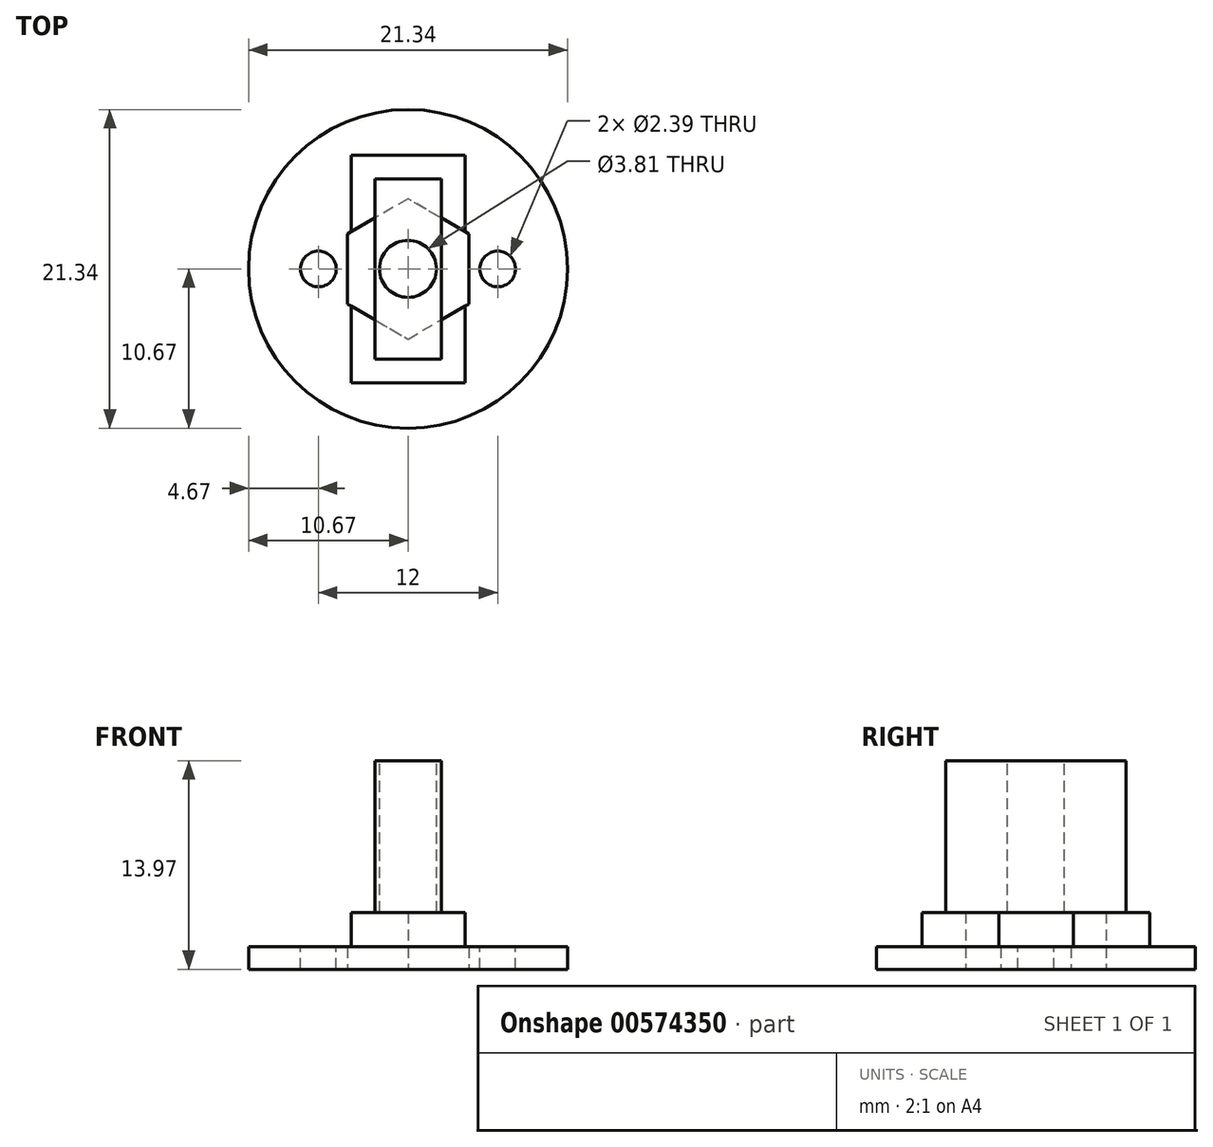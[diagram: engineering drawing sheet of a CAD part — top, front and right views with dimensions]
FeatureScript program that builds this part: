
annotation { "Feature Type Name" : "Feature", "Feature Type Description" : "" }
export const myFeature = defineFeature(function(context is Context, id is Id, definition is map)
    precondition{}
    {
        {
            var Q0;
            Q0=qCreatedBy(makeId("Top.planeOp"),FACE);
            var sketch = newSketch(context, id + "F0", { "sketchPlane" : qUnion([Q0])});
            skCircle(sketch, "E0", {"center": v(0, 0) * mm, "radius": 10.67 * mm});
            skSolve(sketch);
        }
        {
            var Q0;
            Q0 = qSketchRegion(id + "F0", true);
            extrude(context, id + "F1", {"entities" : qUnion([Q0]), "depth" : 1.5 * mm, "offsetDistance" : 25.4 * mm});
        }
        {
            var Q0;
            Q0=makeQuery(id+"F1.opExtrude","CAP_FACE",FACE,{"disambiguationData":[OSD([sQuery(id+"F0.wireOp",EDGE,"E0")])],"isStart":false});
            var sketch = newSketch(context, id + "F2", { "sketchPlane" : qUnion([Q0])});
            skLineSegment(sketch, "E1.bottom", {"start": v(-3.81, 7.62) * mm, "end": v(3.8, 7.62) * mm});
            skLineSegment(sketch, "E1.top", {"start": v(-3.81, -7.62) * mm, "end": v(3.81, -7.62) * mm});
            skLineSegment(sketch, "E1.left", {"start": v(-3.8, 7.62) * mm, "end": v(-3.81, -7.62) * mm});
            skLineSegment(sketch, "E1.right", {"start": v(3.81, 7.62) * mm, "end": v(3.8, -7.62) * mm});
            skLineSegment(sketch, "E2", {"start": v(0, 7.62) * mm, "end": v(0, -7.62) * mm, "construction": true});
            skLineSegment(sketch, "E3", {"start": v(-3.8, 0) * mm, "end": v(3.81, 0) * mm, "construction": true});
            skSolve(sketch);
        }
        {
            var Q0;
            Q0=makeQuery(id+"F2.imprint","IMPRINT",FACE,{"disambiguationData":[TD([[makeQuery(id+"F2.imprint","IMPRINT",EDGE,{"derivedFrom":sQuery(id+"F2.wireOp",EDGE,"E1.bottom")}),-1.0]])]});
            extrude(context, id + "F3", {"entities" : qUnion([Q0]), "operationType" : NewBodyOperationType.ADD, "depth" : 3.8 * mm - 1.5 * mm, "offsetDistance" : 25.4 * mm});
        }
        {
            var Q0;
            Q0=makeQuery(id+"F3.opExtrude","CAP_FACE",FACE,{"disambiguationData":[OSD([sQuery(id+"F2.wireOp",EDGE,"E1.bottom"),sQuery(id+"F2.wireOp",EDGE,"E1.top"),sQuery(id+"F2.wireOp",EDGE,"E1.left"),sQuery(id+"F2.wireOp",EDGE,"E1.right")])],"isStart":false});
            var sketch = newSketch(context, id + "F4", { "sketchPlane" : qUnion([Q0])});
            skLineSegment(sketch, "E4.bottom", {"start": v(-2.22, 6.03) * mm, "end": v(2.22, 6.03) * mm});
            skLineSegment(sketch, "E4.top", {"start": v(-2.22, -6.03) * mm, "end": v(2.22, -6.03) * mm});
            skLineSegment(sketch, "E4.left", {"start": v(-2.22, 6.03) * mm, "end": v(-2.22, -6.03) * mm});
            skLineSegment(sketch, "E4.right", {"start": v(2.22, 6.03) * mm, "end": v(2.22, -6.03) * mm});
            skLineSegment(sketch, "E5", {"start": v(0, 6.03) * mm, "end": v(0, 0) * mm, "construction": true});
            skLineSegment(sketch, "E6", {"start": v(0, 0) * mm, "end": v(-2.22, 0) * mm, "construction": true});
            skSolve(sketch);
        }
        {
            var Q0;
            Q0 = qSketchRegion(id + "F4", true);
            extrude(context, id + "F5", {"entities" : qUnion([Q0]), "operationType" : NewBodyOperationType.ADD, "depth" : 10.16 * mm, "offsetDistance" : 25.4 * mm});
        }
        {
            var Q0;
            Q0=makeQuery(id+"F5.opExtrude","CAP_FACE",FACE,{"disambiguationData":[OSD([sQuery(id+"F4.wireOp",EDGE,"E4.bottom"),sQuery(id+"F4.wireOp",EDGE,"E4.top"),sQuery(id+"F4.wireOp",EDGE,"E4.left"),sQuery(id+"F4.wireOp",EDGE,"E4.right")])],"isStart":false});
            var sketch = newSketch(context, id + "F6", { "sketchPlane" : qUnion([Q0])});
            skCircle(sketch, "E7", {"center": v(0, 0) * mm, "radius": 1.9 * mm});
            skSolve(sketch);
        }
        {
            var Q0;
            Q0 = qSketchRegion(id + "F6", true);
            extrude(context, id + "F7", {"entities" : qUnion([Q0]), "operationType" : NewBodyOperationType.REMOVE, "endBound" : BoundingType.THROUGH_ALL, "oppositeDirection" : true, "depth" : 25.4 * mm, "offsetDistance" : 25.4 * mm});
        }
        {
            var Q0;
            Q0=makeQuery(id+"F1.opExtrude","CAP_FACE",FACE,{"disambiguationData":[OSD([sQuery(id+"F0.wireOp",EDGE,"E0")])],"isStart":true});
            var sketch = newSketch(context, id + "F8", { "sketchPlane" : qUnion([Q0])});
            skCircle(sketch, "E8.cCircle", {"center": v(0, 0) * mm, "radius": 4.06 * mm, "construction": true});
            skLineSegment(sketch, "E8.0", {"start": v(0, 4.7) * mm, "end": v(4.06, 2.35) * mm});
            skLineSegment(sketch, "E8.1", {"start": v(4.06, 2.35) * mm, "end": v(4.06, -2.35) * mm});
            skLineSegment(sketch, "E8.2", {"start": v(4.06, -2.35) * mm, "end": v(0, -4.7) * mm});
            skLineSegment(sketch, "E8.3", {"start": v(0, -4.7) * mm, "end": v(-4.06, -2.35) * mm});
            skLineSegment(sketch, "E8.4", {"start": v(-4.06, -2.35) * mm, "end": v(-4.06, 2.35) * mm});
            skLineSegment(sketch, "E8.5", {"start": v(-4.06, 2.35) * mm, "end": v(0, 4.7) * mm});
            skPoint(sketch, "E8.0.midPoint", {"position": v(2.03, 3.52) * mm});
            skSolve(sketch);
        }
        {
            var Q0;
            Q0=makeQuery(id+"F8.imprint","IMPRINT",FACE,{"disambiguationData":[TD([[makeQuery(id+"F8.imprint","IMPRINT",EDGE,{"derivedFrom":makeQuery(id+"F7.boolean.opBoolean","INTERSECT",EDGE,{"derivedFrom":[makeQuery(id+"F1.opExtrude","CAP_FACE",FACE,{"disambiguationData":[OSD([sQuery(id+"F0.wireOp",EDGE,"E0")])],"isStart":true}),makeQuery(id+"F7.opExtrude","SWEPT_FACE",FACE,{"disambiguationData":[OSD([sQuery(id+"F6.wireOp",EDGE,"E7")])]})]})}),-1.0]])]});
            var Q1;
            Q1=makeQuery(id+"F8.imprint","IMPRINT",FACE,{"disambiguationData":[TD([[makeQuery(id+"F8.imprint","IMPRINT",EDGE,{"derivedFrom":sQuery(id+"F8.wireOp",EDGE,"E8.0")}),-1.0]])]});
            extrude(context, id + "F9", {"entities" : qUnion([Q0, Q1]), "operationType" : NewBodyOperationType.REMOVE, "oppositeDirection" : true, "depth" : 3.8 * mm, "offsetDistance" : 25.4 * mm});
        }
        {
            var Q0;
            Q0=makeQuery(id+"F1.opExtrude","CAP_FACE",FACE,{"disambiguationData":[OSD([sQuery(id+"F0.wireOp",EDGE,"E0")])],"isStart":false});
            var sketch = newSketch(context, id + "F10", { "sketchPlane" : qUnion([Q0])});
            skCircle(sketch, "E9", {"center": v(-6, 0) * mm, "radius": 1.2 * mm});
            skCircle(sketch, "E10", {"center": v(6, 0) * mm, "radius": 1.2 * mm});
            skSolve(sketch);
        }
        {
            var Q0;
            Q0 = qSketchRegion(id + "F10", true);
            extrude(context, id + "F11", {"entities" : qUnion([Q0]), "operationType" : NewBodyOperationType.REMOVE, "endBound" : BoundingType.THROUGH_ALL, "oppositeDirection" : true, "depth" : 25.4 * mm, "offsetDistance" : 25.4 * mm});
        }
    });
